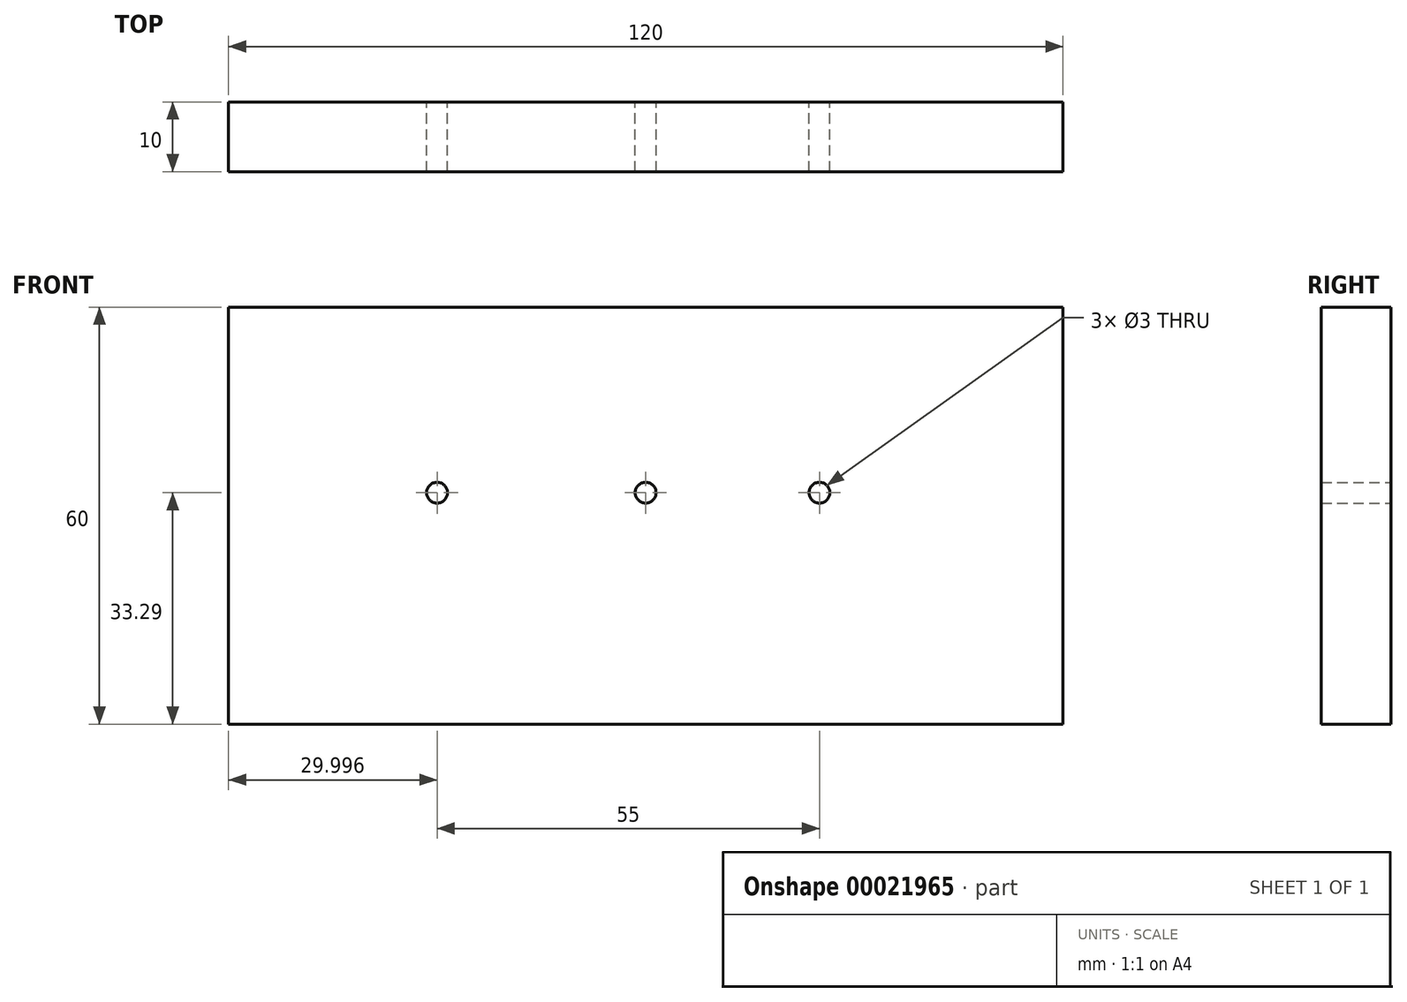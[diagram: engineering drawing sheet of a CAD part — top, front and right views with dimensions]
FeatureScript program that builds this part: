
annotation { "Feature Type Name" : "Feature", "Feature Type Description" : "" }
export const myFeature = defineFeature(function(context is Context, id is Id, definition is map)
    precondition{}
    {
        {
            var Q0;
            Q0=qCreatedBy(makeId("Front.planeOp"),FACE);
            var sketch = newSketch(context, id + "F0", { "sketchPlane" : qUnion([Q0])});
            skLineSegment(sketch, "E0.bottom", {"start": v(-58.97, 26.71) * mm, "end": v(61.03, 26.71) * mm});
            skLineSegment(sketch, "E0.top", {"start": v(-58.97, -33.29) * mm, "end": v(61.03, -33.29) * mm});
            skLineSegment(sketch, "E0.left", {"start": v(-58.97, 26.71) * mm, "end": v(-58.97, -33.29) * mm});
            skLineSegment(sketch, "E0.right", {"start": v(61.03, 26.71) * mm, "end": v(61.03, -33.29) * mm});
            skCircle(sketch, "E1", {"center": v(-28.97, 0) * mm, "radius": 1.5 * mm});
            skCircle(sketch, "E2", {"center": v(1.03, 0) * mm, "radius": 1.5 * mm});
            skCircle(sketch, "E3", {"center": v(26.03, 0) * mm, "radius": 1.5 * mm});
            skLineSegment(sketch, "E4", {"start": v(-41.8, 26.71) * mm, "end": v(-41.8, -33.29) * mm});
            skSolve(sketch);
        }
        {
            var Q0;
            {var subQ1=sQuery(id+"F0.wireOp",EDGE,"E0.left");Q0=makeQuery(id+"F0.imprint","IMPRINT",FACE,{"disambiguationData":[TD([[makeQuery(id+"F0.imprint","IMPRINT",EDGE,{"derivedFrom":subQ1}),1.0]])]});}
            var Q1;
            {var subQ1=sQuery(id+"F0.wireOp",EDGE,"E0.right");Q1=makeQuery(id+"F0.imprint","IMPRINT",FACE,{"disambiguationData":[TD([[makeQuery(id+"F0.imprint","IMPRINT",EDGE,{"derivedFrom":subQ1}),-1.0]])]});}
            extrude(context, id + "F1", {"entities" : qUnion([Q0, Q1]), "depth" : 10 * mm});
        }
    });
